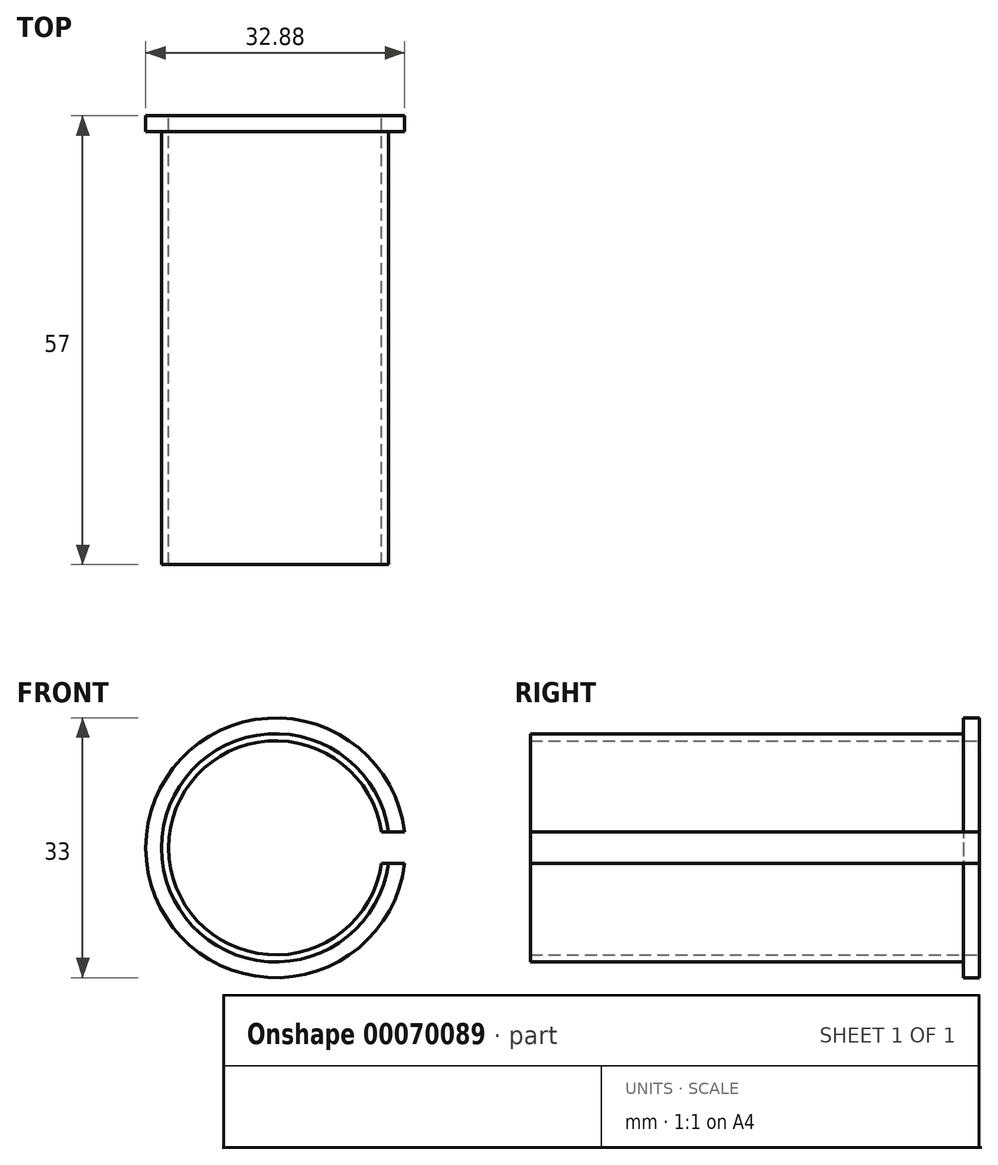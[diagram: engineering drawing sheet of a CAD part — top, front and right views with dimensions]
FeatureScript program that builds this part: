
annotation { "Feature Type Name" : "Feature", "Feature Type Description" : "" }
export const myFeature = defineFeature(function(context is Context, id is Id, definition is map)
    precondition{}
    {
        {
            var Q0;
            Q0=qCreatedBy(makeId("Front.planeOp"),FACE);
            var sketch = newSketch(context, id + "F0", { "sketchPlane" : qUnion([Q0])});
            skCircle(sketch, "E0", {"center": v(0, 0) * mm, "radius": 13.6 * mm});
            skCircle(sketch, "E1", {"center": v(0, 0) * mm, "radius": 14.5 * mm});
            skCircle(sketch, "E2", {"center": v(0, 0) * mm, "radius": 16.5 * mm});
            skLineSegment(sketch, "E3.bottom", {"start": v(19.98, -2) * mm, "end": v(7.98, -2) * mm});
            skLineSegment(sketch, "E3.top", {"start": v(19.98, 2) * mm, "end": v(7.98, 2) * mm});
            skLineSegment(sketch, "E3.left", {"start": v(19.98, -2) * mm, "end": v(19.98, 2) * mm});
            skLineSegment(sketch, "E3.right", {"start": v(7.98, -2) * mm, "end": v(7.98, 2) * mm});
            skLineSegment(sketch, "E4", {"start": v(7.98, 0) * mm, "end": v(19.98, 0) * mm, "construction": true});
            skSolve(sketch);
        }
        {
            var Q0;
            Q0=makeQuery(id+"F0.imprint","IMPRINT",FACE,{"disambiguationData":[TD([[makeQuery(id+"F0.imprint","IMPRINT",EDGE,{"derivedFrom":sQuery(id+"F0.wireOp",EDGE,"E1")}),-1.0]])]});
            extrude(context, id + "F1", {"entities" : qUnion([Q0]), "depth" : 2 * mm});
        }
        {
            var Q0;
            Q0=makeQuery(id+"F0.imprint","IMPRINT",FACE,{"disambiguationData":[TD([[makeQuery(id+"F0.imprint","IMPRINT",EDGE,{"derivedFrom":sQuery(id+"F0.wireOp",EDGE,"E0")}),-1.0]])]});
            extrude(context, id + "F2", {"entities" : qUnion([Q0]), "operationType" : NewBodyOperationType.ADD, "depth" : 57 * mm});
        }
        {
            var Q0;
            {var subQ5=sQuery(id+"F0.wireOp",EDGE,"E3.left");Q0=makeQuery(id+"F0.imprint","IMPRINT",FACE,{"disambiguationData":[TD([[makeQuery(id+"F0.imprint","IMPRINT",EDGE,{"derivedFrom":subQ5}),1.0]])]});}
            var Q1;
            {var subQ0=sQuery(id+"F0.wireOp",EDGE,"E3.bottom");var subQ1=sQuery(id+"F0.wireOp",EDGE,"E1");var subQ2=makeQuery(id+"F0.imprint","INTERSECT",VERTEX,{"derivedFrom":[subQ1,subQ0]});Q1=makeQuery(id+"F0.imprint","IMPRINT",FACE,{"disambiguationData":[TD([[makeQuery(id+"F0.imprint","IMPRINT",EDGE,{"disambiguationData":[TD([[subQ2,-1.0]])],"derivedFrom":subQ1}),-1.0]])]});}
            var Q2;
            {var subQ0=sQuery(id+"F0.wireOp",EDGE,"E3.bottom");var subQ1=sQuery(id+"F0.wireOp",EDGE,"E0");var subQ2=makeQuery(id+"F0.imprint","INTERSECT",VERTEX,{"derivedFrom":[subQ1,subQ0]});Q2=makeQuery(id+"F0.imprint","IMPRINT",FACE,{"disambiguationData":[TD([[makeQuery(id+"F0.imprint","IMPRINT",EDGE,{"disambiguationData":[TD([[subQ2,-1.0]])],"derivedFrom":subQ1}),-1.0]])]});}
            var Q3;
            {var subQ5=sQuery(id+"F0.wireOp",EDGE,"E3.right");Q3=makeQuery(id+"F0.imprint","IMPRINT",FACE,{"disambiguationData":[TD([[makeQuery(id+"F0.imprint","IMPRINT",EDGE,{"derivedFrom":subQ5}),-1.0]])]});}
            extrude(context, id + "F3", {"entities" : qUnion([Q0, Q1, Q2, Q3]), "operationType" : NewBodyOperationType.REMOVE, "depth" : 127 * mm});
        }
    });
